# Revit family: Rohrschelle Titan HD, halb Zoll, Silikon
name_source: partatom
category: HLS-Bauteile
revit_build: Autodesk Revit 2017 (Build: 20190507_1515(x64)
units: mm (PartAtom-declared; Revit-internal decimal feet)

## family parameters
Arbeitsebenenbasiert = Ja
Beim Laden mit Abzugskörper schneiden = Nein
Bemaßung runder Anschluss = Durchmesser verwenden
Gemeinsam genutzt = Ja
Immer vertikal = Nein
Raumberechnungspunkt = Nein
Teiletyp = Normal

## types (30) — shared parameters
A = 26 mm  [stored 0.0853018 ft]
DF1 = 29 mm  [stored 0.0951444 ft]
DS = 6 mm  [stored 0.019685 ft]
DVS = 13 mm
Firma = MEFA Befestigungs- und Montagesysteme GmbH
HGA = 15 mm  [stored 0.0492126 ft]
MB = 50 mm  [stored 0.164042 ft]
MD = 5 mm  [stored 0.0164042 ft]
Vorgabe-Ansicht = 1219 mm
max. zul. Last horizontal = 0.00 kN
max. zul. Last vertikal = 0.00 kN
zero-valued in all types: Nennweite DN Rohr, Stärke Material, max. Rohraußendurchmesser, min. Rohraußendurchmesser

## per-type parameters (varying)
- Titan HD, 1/2", Ø 64, Silikon: Achsabstand=125 mm; Anschluss=1/2''; Anschlußhöhe=26 mm; Artikelnummer=0077506; B=154 mm; Bauart=zweiteilig; Baustoffklasse=B2; Brandschutz=RAL GZ 656; Breite=154 mm; D=64 mm  [stored 0.209974 ft]; D0=76 mm  [stored 0.249344 ft]; DF2=19 mm  [stored 0.062336 ft]; Dämmstärke=6 mm  [stored 0.019685 ft]; EAN=4250928405203; Fabrikat=MEFA; Farbe Schalldämmeinlage=rot; Gewicht=0.93 kg; Gewicht pro Bauteil=0.93 kg; H=101 mm; Höhe=101 mm; Kurztext1=Rohrschelle Titan HD 50x5,0; Kurztext2=64 mm 1/2'' Silikon; Material=Stahl; Material Schalldämmeinlage=Silikon; Materialmaße=50x5,0 mm; Materialname=S235; Mengeneinheit=St; Oberflaeche=galvanisch verzinkt; R=38 mm  [stored 0.124672 ft]; RM=43 mm; Rohraußendurchmesser=64 mm  [stored 0.209974 ft]; Rohraußendurchmesser Zoll=Zoll; S=125 mm; Schalldämmeinlage=Silikon; Verschluss=Schraubverschluss; Verschluss-Schraube=M12; max. Höhe=101 mm; max. Temperaturbeständigkeit=250 °C; max. zul. Last=3.20 kN; vpe=1 St
- Titan HD, 1/2", Ø 76, Silikon: Achsabstand=137 mm; Anschluss=1/2''; Anschlußhöhe=26 mm; Artikelnummer=0077510; B=166 mm; Bauart=zweiteilig; Baustoffklasse=B2; Brandschutz=RAL GZ 656; Breite=166 mm; D=76 mm  [stored 0.249344 ft]; D0=88 mm  [stored 0.288714 ft]; DF2=19 mm  [stored 0.062336 ft]; Dämmstärke=6 mm  [stored 0.019685 ft]; EAN=4250928405210; Fabrikat=MEFA; Farbe Schalldämmeinlage=rot; Gewicht=1.02 kg; Gewicht pro Bauteil=1.02 kg; H=113 mm; Höhe=113 mm; Kurztext1=Rohrschelle Titan HD 50x5,0; Kurztext2=76 mm 1/2'' Silikon; Material=Stahl; Material Schalldämmeinlage=Silikon; Materialmaße=50x5,0 mm; Materialname=S235; Mengeneinheit=St; Oberflaeche=galvanisch verzinkt; R=44 mm  [stored 0.144357 ft]; RM=49 mm; Rohraußendurchmesser=76 mm  [stored 0.249344 ft]; Rohraußendurchmesser Zoll=2 1/2 Zoll; S=137 mm; Schalldämmeinlage=Silikon; Verschluss=Schraubverschluss; Verschluss-Schraube=M12; max. Höhe=113 mm; max. Temperaturbeständigkeit=250 °C; max. zul. Last=3.20 kN; vpe=1 St
- Titan HD, 1/2", Ø 89, Silikon: Artikelnummer=0077512; B=179 mm; Breite=0 mm  [stored 0 ft]; D=89 mm  [stored 0.291995 ft]; D0=101 mm; DF2=19 mm  [stored 0.062336 ft]; Dämmstärke=0 mm  [stored 0 ft]; Gewicht=0.00 kg; Gewicht pro Bauteil=0.00 kg; H=126 mm; R=51 mm; RM=56 mm; Rohraußendurchmesser=0 mm  [stored 0 ft]; S=150 mm; max. Höhe=0 mm  [stored 0 ft]; max. zul. Last=0.00 kN
- Titan HD, 1/2", Ø108, Silikon: Achsabstand=170 mm; Anschluss=1/2''; Anschlußhöhe=26 mm; Artikelnummer=0077518; B=199 mm; Bauart=zweiteilig; Baustoffklasse=B2; Brandschutz=RAL GZ 656; Breite=199 mm; D=108 mm; D0=120 mm; DF2=20 mm  [stored 0.0656168 ft]; Dämmstärke=6 mm  [stored 0.019685 ft]; EAN=4250928405234; Fabrikat=MEFA; Farbe Schalldämmeinlage=rot; Gewicht=1.26 kg; Gewicht pro Bauteil=1.26 kg; H=145 mm; Höhe=145 mm; Kurztext1=Rohrschelle Titan HD 50x5,0; Kurztext2=108 mm 1/2'' Silikon; Material=Stahl; Material Schalldämmeinlage=Silikon; Materialmaße=50x5,0 mm; Materialname=S235; Mengeneinheit=St; Oberflaeche=galvanisch verzinkt; R=60 mm  [stored 0.19685 ft]; RM=65 mm; Rohraußendurchmesser=108 mm; Rohraußendurchmesser Zoll=Zoll; S=170 mm; Schalldämmeinlage=Silikon; Verschluss=Schraubverschluss; Verschluss-Schraube=M12; max. Höhe=145 mm; max. Temperaturbeständigkeit=250 °C; max. zul. Last=3.20 kN; vpe=1 St
- Titan HD, 1/2", Ø110, Silikon: Achsabstand=172 mm; Anschluss=1/2''; Anschlußhöhe=26 mm; Artikelnummer=0077534; B=201 mm; Bauart=zweiteilig; Baustoffklasse=B2; Brandschutz=RAL GZ 656; Breite=201 mm; D=110 mm; D0=122 mm; DF2=20 mm  [stored 0.0656168 ft]; Dämmstärke=6 mm  [stored 0.019685 ft]; EAN=4250928405241; Fabrikat=MEFA; Farbe Schalldämmeinlage=rot; Gewicht=1.28 kg; Gewicht pro Bauteil=1.28 kg; H=147 mm; Höhe=147 mm; Kurztext1=Rohrschelle Titan HD 50x5,0; Kurztext2=110 mm 1/2'' Silikon; Material=Stahl; Material Schalldämmeinlage=Silikon; Materialmaße=50x5,0 mm; Materialname=S235; Mengeneinheit=St; Oberflaeche=galvanisch verzinkt; R=61 mm  [stored 0.200131 ft]; RM=66 mm; Rohraußendurchmesser=110 mm; Rohraußendurchmesser Zoll=Zoll; S=172 mm; Schalldämmeinlage=Silikon; Verschluss=Schraubverschluss; Verschluss-Schraube=M12; max. Höhe=147 mm; max. Temperaturbeständigkeit=250 °C; max. zul. Last=3.20 kN; vpe=1 St
- Titan HD, 1/2", Ø133, Silikon: Achsabstand=195 mm; Anschluss=1/2''; Anschlußhöhe=26 mm; Artikelnummer=0077607; B=224 mm; Bauart=zweiteilig; Baustoffklasse=B2; Brandschutz=RAL GZ 656; Breite=224 mm; D=133 mm; D0=145 mm; DF2=20 mm  [stored 0.0656168 ft]; Dämmstärke=6 mm  [stored 0.019685 ft]; EAN=4250928405289; Fabrikat=MEFA; Farbe Schalldämmeinlage=rot; Gewicht=1.45 kg; Gewicht pro Bauteil=1.45 kg; H=170 mm; Höhe=170 mm; Kurztext1=Rohrschelle Titan HD 50x5,0; Kurztext2=133 mm 1/2'' Silikon; Material=Stahl; Material Schalldämmeinlage=Silikon; Materialmaße=50x5,0 mm; Materialname=S235; Mengeneinheit=St; Oberflaeche=galvanisch verzinkt; R=73 mm; RM=78 mm; Rohraußendurchmesser=133 mm; Rohraußendurchmesser Zoll=Zoll; S=195 mm; Schalldämmeinlage=Silikon; Verschluss=Schraubverschluss; Verschluss-Schraube=M12; max. Höhe=170 mm; max. Temperaturbeständigkeit=250 °C; max. zul. Last=3.20 kN; vpe=1 St
- Titan HD, 1/2", Ø135, Silikon: Achsabstand=197 mm; Anschluss=1/2''; Anschlußhöhe=26 mm; Artikelnummer=0077615; B=226 mm; Bauart=zweiteilig; Baustoffklasse=B2; Brandschutz=RAL GZ 656; Breite=226 mm; D=135 mm; D0=147 mm; DF2=20 mm  [stored 0.0656168 ft]; Dämmstärke=6 mm  [stored 0.019685 ft]; EAN=4250928405296; Fabrikat=MEFA; Farbe Schalldämmeinlage=rot; Gewicht=1.46 kg; Gewicht pro Bauteil=1.46 kg; H=172 mm; Höhe=172 mm; Kurztext1=Rohrschelle Titan HD 50x5,0; Kurztext2=135 mm 1/2'' Silikon; Material=Stahl; Material Schalldämmeinlage=Silikon; Materialmaße=50x5,0 mm; Materialname=S235; Mengeneinheit=St; Oberflaeche=galvanisch verzinkt; R=74 mm; RM=79 mm; Rohraußendurchmesser=135 mm; Rohraußendurchmesser Zoll=Zoll; S=197 mm; Schalldämmeinlage=Silikon; Verschluss=Schraubverschluss; Verschluss-Schraube=M12; max. Höhe=172 mm; max. Temperaturbeständigkeit=250 °C; max. zul. Last=3.20 kN; vpe=1 St
- Titan HD, 1/2", Ø140, Silikon: Achsabstand=202 mm; Anschluss=1/2''; Anschlußhöhe=26 mm; Artikelnummer=0077623; B=231 mm; Bauart=zweiteilig; Baustoffklasse=B2; Brandschutz=RAL GZ 656; Breite=231 mm; D=140 mm; D0=152 mm; DF2=20 mm  [stored 0.0656168 ft]; Dämmstärke=6 mm  [stored 0.019685 ft]; EAN=4250928405302; Fabrikat=MEFA; Farbe Schalldämmeinlage=rot; Gewicht=1.50 kg; Gewicht pro Bauteil=1.50 kg; H=177 mm; Höhe=177 mm; Kurztext1=Rohrschelle Titan HD 50x5,0; Kurztext2=140 mm 1/2'' Silikon; Material=Stahl; Material Schalldämmeinlage=Silikon; Materialmaße=50x5,0 mm; Materialname=S235; Mengeneinheit=St; Oberflaeche=galvanisch verzinkt; R=76 mm  [stored 0.249344 ft]; RM=81 mm  [stored 0.265748 ft]; Rohraußendurchmesser=140 mm; Rohraußendurchmesser Zoll=5 Zoll; S=202 mm; Schalldämmeinlage=Silikon; Verschluss=Schraubverschluss; Verschluss-Schraube=M12; max. Höhe=177 mm; max. Temperaturbeständigkeit=250 °C; max. zul. Last=3.20 kN; vpe=1 St
- Titan HD, 1/2", Ø160, Silikon: Achsabstand=222 mm; Anschluss=1/2''; Anschlußhöhe=26 mm; Artikelnummer=0077682; B=251 mm; Bauart=zweiteilig; Baustoffklasse=B2; Brandschutz=RAL GZ 656; Breite=251 mm; D=160 mm; D0=172 mm; DF2=20 mm  [stored 0.0656168 ft]; Dämmstärke=6 mm  [stored 0.019685 ft]; EAN=4250928405326; Fabrikat=MEFA; Farbe Schalldämmeinlage=rot; Gewicht=1.65 kg; Gewicht pro Bauteil=1.65 kg; H=197 mm; Höhe=197 mm; Kurztext1=Rohrschelle Titan HD 50x5,0; Kurztext2=160 mm 1/2'' Silikon; Material=Stahl; Material Schalldämmeinlage=Silikon; Materialmaße=50x5,0 mm; Materialname=S235; Mengeneinheit=St; Oberflaeche=galvanisch verzinkt; R=86 mm  [stored 0.282152 ft]; RM=91 mm  [stored 0.298556 ft]; Rohraußendurchmesser=160 mm; Rohraußendurchmesser Zoll=Zoll; S=222 mm; Schalldämmeinlage=Silikon; Verschluss=Schraubverschluss; Verschluss-Schraube=M12; max. Höhe=197 mm; max. Temperaturbeständigkeit=250 °C; max. zul. Last=3.20 kN; vpe=1 St
- Titan HD, 1/2", Ø165, Silikon: Achsabstand=227 mm; Anschluss=1/2''; Anschlußhöhe=26 mm; Artikelnummer=0077690; B=256 mm; Bauart=zweiteilig; Baustoffklasse=B2; Brandschutz=RAL GZ 656; Breite=256 mm; D=165 mm; D0=177 mm; DF2=20 mm  [stored 0.0656168 ft]; Dämmstärke=6 mm  [stored 0.019685 ft]; EAN=4250928405333; Fabrikat=MEFA; Farbe Schalldämmeinlage=rot; Gewicht=1.69 kg; Gewicht pro Bauteil=1.69 kg; H=202 mm; Höhe=202 mm; Kurztext1=Rohrschelle Titan HD 50x5,0; Kurztext2=165 mm 1/2'' Silikon; Material=Stahl; Material Schalldämmeinlage=Silikon; Materialmaße=50x5,0 mm; Materialname=S235; Mengeneinheit=St; Oberflaeche=galvanisch verzinkt; R=89 mm  [stored 0.291995 ft]; RM=94 mm; Rohraußendurchmesser=165 mm; Rohraußendurchmesser Zoll=6 Zoll; S=227 mm; Schalldämmeinlage=Silikon; Verschluss=Schraubverschluss; Verschluss-Schraube=M12; max. Höhe=202 mm; max. Temperaturbeständigkeit=250 °C; max. zul. Last=3.20 kN; vpe=1 St
- Titan HD, 1/2", Ø168, Silikon: Achsabstand=230 mm; Anschluss=1/2''; Anschlußhöhe=26 mm; Artikelnummer=0077712; B=259 mm; Bauart=zweiteilig; Baustoffklasse=B2; Brandschutz=RAL GZ 656; Breite=259 mm; D=168 mm; D0=180 mm; DF2=20 mm  [stored 0.0656168 ft]; Dämmstärke=6 mm  [stored 0.019685 ft]; EAN=4250928405340; Fabrikat=MEFA; Farbe Schalldämmeinlage=rot; Gewicht=1.71 kg; Gewicht pro Bauteil=1.71 kg; H=205 mm; Höhe=205 mm; Kurztext1=Rohrschelle Titan HD 50x5,0; Kurztext2=168 mm 1/2'' Silikon; Material=Stahl; Material Schalldämmeinlage=Silikon; Materialmaße=50x5,0 mm; Materialname=S235; Mengeneinheit=St; Oberflaeche=galvanisch verzinkt; R=90 mm; RM=95 mm; Rohraußendurchmesser=168 mm; Rohraußendurchmesser Zoll=Zoll; S=230 mm; Schalldämmeinlage=Silikon; Verschluss=Schraubverschluss; Verschluss-Schraube=M12; max. Höhe=205 mm; max. Temperaturbeständigkeit=250 °C; max. zul. Last=3.20 kN; vpe=1 St
- Titan HD, 1/2", Ø194, Silikon: Achsabstand=257 mm; Anschluss=1/2''; Anschlußhöhe=26 mm; Artikelnummer=0077771; B=286 mm; Bauart=zweiteilig; Baustoffklasse=B2; Brandschutz=RAL GZ 656; Breite=286 mm; D=194 mm; D0=206 mm; DF2=20 mm  [stored 0.0656168 ft]; Dämmstärke=6 mm  [stored 0.019685 ft]; EAN=4250928405371; Fabrikat=MEFA; Farbe Schalldämmeinlage=rot; Gewicht=1.91 kg; Gewicht pro Bauteil=1.91 kg; H=231 mm; Höhe=231 mm; Kurztext1=Rohrschelle Titan HD 50x5,0; Kurztext2=194 mm 1/2'' Silikon; Material=Stahl; Material Schalldämmeinlage=Silikon; Materialmaße=50x5,0 mm; Materialname=S235; Mengeneinheit=St; Oberflaeche=galvanisch verzinkt; R=103 mm; RM=108 mm; Rohraußendurchmesser=194 mm; Rohraußendurchmesser Zoll=Zoll; S=257 mm; Schalldämmeinlage=Silikon; Verschluss=Schraubverschluss; Verschluss-Schraube=M12; max. Höhe=231 mm; max. Temperaturbeständigkeit=250 °C; max. zul. Last=11.50 kN; vpe=1 St
- Titan HD, 1/2", Ø200, Silikon: Achsabstand=263 mm; Anschluss=1/2''; Anschlußhöhe=26 mm; Artikelnummer=0077798; B=292 mm; Bauart=zweiteilig; Baustoffklasse=B2; Brandschutz=RAL GZ 656; Breite=292 mm; D=200 mm; D0=212 mm; DF2=20 mm  [stored 0.0656168 ft]; Dämmstärke=6 mm  [stored 0.019685 ft]; EAN=4250928405388; Fabrikat=MEFA; Farbe Schalldämmeinlage=rot; Gewicht=1.95 kg; Gewicht pro Bauteil=1.95 kg; H=237 mm; Höhe=237 mm; Kurztext1=Rohrschelle Titan HD 50x5,0; Kurztext2=200 mm 1/2'' Silikon; Material=Stahl; Material Schalldämmeinlage=Silikon; Materialmaße=50x5,0 mm; Materialname=S235; Mengeneinheit=St; Oberflaeche=galvanisch verzinkt; R=106 mm; RM=111 mm; Rohraußendurchmesser=200 mm; Rohraußendurchmesser Zoll=Zoll; S=263 mm; Schalldämmeinlage=Silikon; Verschluss=Schraubverschluss; Verschluss-Schraube=M12; max. Höhe=237 mm; max. Temperaturbeständigkeit=250 °C; max. zul. Last=11.50 kN; vpe=1 St
- Titan HD, 1/2", Ø210, Silikon: Achsabstand=273 mm; Anschluss=1/2''; Anschlußhöhe=26 mm; Artikelnummer=0077801; B=302 mm; Bauart=zweiteilig; Baustoffklasse=B2; Brandschutz=RAL GZ 656; Breite=302 mm; D=210 mm; D0=222 mm; DF2=20 mm  [stored 0.0656168 ft]; Dämmstärke=6 mm  [stored 0.019685 ft]; EAN=4250928405395; Fabrikat=MEFA; Farbe Schalldämmeinlage=rot; Gewicht=2.03 kg; Gewicht pro Bauteil=2.03 kg; H=247 mm; Höhe=247 mm; Kurztext1=Rohrschelle Titan HD 50x5,0; Kurztext2=210 mm 1/2'' Silikon; Material=Stahl; Material Schalldämmeinlage=Silikon; Materialmaße=50x5,0 mm; Materialname=S235; Mengeneinheit=St; Oberflaeche=galvanisch verzinkt; R=111 mm; RM=116 mm; Rohraußendurchmesser=210 mm; Rohraußendurchmesser Zoll=Zoll; S=273 mm; Schalldämmeinlage=Silikon; Verschluss=Schraubverschluss; Verschluss-Schraube=M12; max. Höhe=247 mm; max. Temperaturbeständigkeit=250 °C; max. zul. Last=11.50 kN; vpe=1 St
- Titan HD, 1/2", Ø219, Silikon: Achsabstand=282 mm; Anschluss=1/2''; Anschlußhöhe=26 mm; Artikelnummer=0077828; B=311 mm; Bauart=zweiteilig; Baustoffklasse=B2; Brandschutz=RAL GZ 656; Breite=311 mm; D=219 mm; D0=231 mm; DF2=20 mm  [stored 0.0656168 ft]; Dämmstärke=6 mm  [stored 0.019685 ft]; EAN=4250928405401; Fabrikat=MEFA; Farbe Schalldämmeinlage=rot; Gewicht=2.09 kg; Gewicht pro Bauteil=2.09 kg; H=256 mm; Höhe=256 mm; Kurztext1=Rohrschelle Titan HD 50x5,0; Kurztext2=219 mm 1/2'' Silikon; Material=Stahl; Material Schalldämmeinlage=Silikon; Materialmaße=50x5,0 mm; Materialname=S235; Mengeneinheit=St; Oberflaeche=galvanisch verzinkt; R=116 mm; RM=121 mm; Rohraußendurchmesser=219 mm; Rohraußendurchmesser Zoll=8 Zoll; S=282 mm; Schalldämmeinlage=Silikon; Verschluss=Schraubverschluss; Verschluss-Schraube=M12; max. Höhe=256 mm; max. Temperaturbeständigkeit=250 °C; max. zul. Last=11.50 kN; vpe=1 St
- Titan HD, 1/2", Ø267, Silikon: Achsabstand=330 mm; Anschluss=1/2''; Anschlußhöhe=26 mm; Artikelnummer=0077895; B=359 mm; Bauart=zweiteilig; Baustoffklasse=B2; Brandschutz=RAL GZ 656; Breite=359 mm; D=267 mm; D0=279 mm; DF2=20 mm  [stored 0.0656168 ft]; Dämmstärke=6 mm  [stored 0.019685 ft]; EAN=4250928405432; Fabrikat=MEFA; Farbe Schalldämmeinlage=rot; Gewicht=2.45 kg; Gewicht pro Bauteil=2.45 kg; H=304 mm; Höhe=304 mm; Kurztext1=Rohrschelle Titan HD 50x5,0; Kurztext2=267 mm 1/2'' Silikon; Material=Stahl; Material Schalldämmeinlage=Silikon; Materialmaße=50x5,0 mm; Materialname=S235; Mengeneinheit=St; Oberflaeche=galvanisch verzinkt; R=140 mm; RM=145 mm; Rohraußendurchmesser=267 mm; Rohraußendurchmesser Zoll=Zoll; S=330 mm; Schalldämmeinlage=Silikon; Verschluss=Schraubverschluss; Verschluss-Schraube=M12; max. Höhe=304 mm; max. Temperaturbeständigkeit=250 °C; max. zul. Last=11.50 kN; vpe=1 St
- Titan HD, 1/2", Ø273, Silikon: Achsabstand=336 mm; Anschluss=1/2''; Anschlußhöhe=26 mm; Artikelnummer=0077909; B=365 mm; Bauart=zweiteilig; Baustoffklasse=B2; Brandschutz=RAL GZ 656; Breite=365 mm; D=273 mm; D0=285 mm; DF2=20 mm  [stored 0.0656168 ft]; Dämmstärke=6 mm  [stored 0.019685 ft]; EAN=4250928405449; Fabrikat=MEFA; Farbe Schalldämmeinlage=rot; Gewicht=2.50 kg; Gewicht pro Bauteil=2.50 kg; H=310 mm; Höhe=310 mm; Kurztext1=Rohrschelle Titan HD 50x5,0; Kurztext2=273 mm 1/2'' Silikon; Material=Stahl; Material Schalldämmeinlage=Silikon; Materialmaße=50x5,0 mm; Materialname=S235; Mengeneinheit=St; Oberflaeche=galvanisch verzinkt; R=143 mm; RM=148 mm; Rohraußendurchmesser=273 mm; Rohraußendurchmesser Zoll=10 Zoll; S=336 mm; Schalldämmeinlage=Silikon; Verschluss=Schraubverschluss; Verschluss-Schraube=M12; max. Höhe=310 mm; max. Temperaturbeständigkeit=250 °C; max. zul. Last=11.50 kN; vpe=1 St
- Titan HD, 1/2", Ø324, Silikon: Achsabstand=387 mm; Anschluss=1/2''; Anschlußhöhe=26 mm; Artikelnummer=0077941; B=416 mm; Bauart=zweiteilig; Baustoffklasse=B2; Brandschutz=RAL GZ 656; Breite=416 mm; D=324 mm; D0=336 mm; DF2=20 mm  [stored 0.0656168 ft]; Dämmstärke=6 mm  [stored 0.019685 ft]; EAN=4250928405470; Fabrikat=MEFA; Farbe Schalldämmeinlage=rot; Gewicht=2.88 kg; Gewicht pro Bauteil=2.88 kg; H=361 mm; Höhe=361 mm; Kurztext1=Rohrschelle Titan HD 50x5,0; Kurztext2=324 mm 1/2'' Silikon; Material=Stahl; Material Schalldämmeinlage=Silikon; Materialmaße=50x5,0 mm; Materialname=S235; Mengeneinheit=St; Oberflaeche=galvanisch verzinkt; R=168 mm; RM=173 mm; Rohraußendurchmesser=324 mm; Rohraußendurchmesser Zoll=12 Zoll; S=387 mm; Schalldämmeinlage=Silikon; Verschluss=Schraubverschluss; Verschluss-Schraube=M12; max. Höhe=361 mm; max. Temperaturbeständigkeit=250 °C; max. zul. Last=11.50 kN; vpe=1 St
- Titan HD, 1/2", Ø356, Silikon: Achsabstand=419 mm; Anschluss=1/2''; Anschlußhöhe=26 mm; Artikelnummer=0077968; B=448 mm; Bauart=zweiteilig; Baustoffklasse=B2; Brandschutz=RAL GZ 656; Breite=448 mm; D=356 mm; D0=368 mm; DF2=20 mm  [stored 0.0656168 ft]; Dämmstärke=6 mm  [stored 0.019685 ft]; EAN=4250928405487; Fabrikat=MEFA; Farbe Schalldämmeinlage=rot; Gewicht=3.12 kg; Gewicht pro Bauteil=3.12 kg; H=393 mm; Höhe=393 mm; Kurztext1=Rohrschelle Titan HD 50x5,0; Kurztext2=356 mm 1/2'' Silikon; Material=Stahl; Material Schalldämmeinlage=Silikon; Materialmaße=50x5,0 mm; Materialname=S235; Mengeneinheit=St; Oberflaeche=galvanisch verzinkt; R=184 mm; RM=189 mm; Rohraußendurchmesser=356 mm; Rohraußendurchmesser Zoll=Zoll; S=419 mm; Schalldämmeinlage=Silikon; Verschluss=Schraubverschluss; Verschluss-Schraube=M12; max. Höhe=393 mm; max. Temperaturbeständigkeit=250 °C; max. zul. Last=11.50 kN; vpe=1 St
- Titan HD, 1/2", Ø368, Silikon: Achsabstand=431 mm; Anschluss=1/2''; Anschlußhöhe=26 mm; Artikelnummer=0077984; B=460 mm; Bauart=zweiteilig; Baustoffklasse=B2; Brandschutz=RAL GZ 656; Breite=460 mm; D=368 mm; D0=380 mm; DF2=20 mm  [stored 0.0656168 ft]; Dämmstärke=6 mm  [stored 0.019685 ft]; EAN=4250928405494; Fabrikat=MEFA; Farbe Schalldämmeinlage=rot; Gewicht=3.21 kg; Gewicht pro Bauteil=3.21 kg; H=405 mm; Höhe=405 mm; Kurztext1=Rohrschelle Titan HD 50x5,0; Kurztext2=368 mm 1/2'' Silikon; Material=Stahl; Material Schalldämmeinlage=Silikon; Materialmaße=50x5,0 mm; Materialname=S235; Mengeneinheit=St; Oberflaeche=galvanisch verzinkt; R=190 mm; RM=195 mm; Rohraußendurchmesser=368 mm; Rohraußendurchmesser Zoll=Zoll; S=431 mm; Schalldämmeinlage=Silikon; Verschluss=Schraubverschluss; Verschluss-Schraube=M12; max. Höhe=405 mm; max. Temperaturbeständigkeit=250 °C; max. zul. Last=11.50 kN; vpe=1 St
- Titan HD, 1/2", Ø114, Silikon: Achsabstand=176 mm; Anschluss=1/2''; Anschlußhöhe=26 mm; Artikelnummer=0077550; B=205 mm; Bauart=zweiteilig; Baustoffklasse=B2; Brandschutz=RAL GZ 656; Breite=205 mm; D=114 mm; D0=126 mm; DF2=20 mm  [stored 0.0656168 ft]; Dämmstärke=6 mm  [stored 0.019685 ft]; EAN=4250928405258; Fabrikat=MEFA; Farbe Schalldämmeinlage=rot; Gewicht=1.31 kg; Gewicht pro Bauteil=1.31 kg; H=151 mm; Höhe=151 mm; Kurztext1=Rohrschelle Titan HD 50x5,0; Kurztext2=114 mm 1/2'' Silikon; Material=Stahl; Material Schalldämmeinlage=Silikon; Materialmaße=50x5,0 mm; Materialname=S235; Mengeneinheit=St; Oberflaeche=galvanisch verzinkt; R=63 mm  [stored 0.206693 ft]; RM=68 mm  [stored 0.223097 ft]; Rohraußendurchmesser=114 mm; Rohraußendurchmesser Zoll=4 Zoll; S=176 mm; Schalldämmeinlage=Silikon; Verschluss=Schraubverschluss; Verschluss-Schraube=M12; max. Höhe=151 mm; max. Temperaturbeständigkeit=250 °C; max. zul. Last=3.20 kN; vpe=1 St
- Titan HD, 1/2", Ø125, Silikon: Achsabstand=187 mm; Anschluss=1/2''; Anschlußhöhe=26 mm; Artikelnummer=0077585; B=216 mm; Bauart=zweiteilig; Baustoffklasse=B2; Brandschutz=RAL GZ 656; Breite=216 mm; D=125 mm; D0=137 mm; DF2=20 mm  [stored 0.0656168 ft]; Dämmstärke=6 mm  [stored 0.019685 ft]; EAN=4250928405265; Fabrikat=MEFA; Farbe Schalldämmeinlage=rot; Gewicht=1.39 kg; Gewicht pro Bauteil=1.39 kg; H=162 mm; Höhe=162 mm; Kurztext1=Rohrschelle Titan HD 50x5,0; Kurztext2=125 mm 1/2'' Silikon; Material=Stahl; Material Schalldämmeinlage=Silikon; Materialmaße=50x5,0 mm; Materialname=S235; Mengeneinheit=St; Oberflaeche=galvanisch verzinkt; R=69 mm; RM=74 mm; Rohraußendurchmesser=125 mm; Rohraußendurchmesser Zoll=Zoll; S=187 mm; Schalldämmeinlage=Silikon; Verschluss=Schraubverschluss; Verschluss-Schraube=M12; max. Höhe=162 mm; max. Temperaturbeständigkeit=250 °C; max. zul. Last=3.20 kN; vpe=1 St
- Titan HD, 1/2", Ø127, Silikon: Achsabstand=189 mm; Anschluss=1/2''; Anschlußhöhe=26 mm; Artikelnummer=0077593; B=218 mm; Bauart=zweiteilig; Baustoffklasse=B2; Brandschutz=RAL GZ 656; Breite=218 mm; D=127 mm; D0=139 mm; DF2=20 mm  [stored 0.0656168 ft]; Dämmstärke=6 mm  [stored 0.019685 ft]; EAN=4250928405272; Fabrikat=MEFA; Farbe Schalldämmeinlage=rot; Gewicht=1.40 kg; Gewicht pro Bauteil=1.40 kg; H=164 mm; Höhe=164 mm; Kurztext1=Rohrschelle Titan HD 50x5,0; Kurztext2=127 mm 1/2'' Silikon; Material=Stahl; Material Schalldämmeinlage=Silikon; Materialmaße=50x5,0 mm; Materialname=S235; Mengeneinheit=St; Oberflaeche=galvanisch verzinkt; R=70 mm; RM=75 mm; Rohraußendurchmesser=127 mm; Rohraußendurchmesser Zoll=Zoll; S=189 mm; Schalldämmeinlage=Silikon; Verschluss=Schraubverschluss; Verschluss-Schraube=M12; max. Höhe=164 mm; max. Temperaturbeständigkeit=250 °C; max. zul. Last=3.20 kN; vpe=1 St
- Titan HD, 1/2", Ø152, Silikon: Achsabstand=214 mm; Anschluss=1/2''; Anschlußhöhe=26 mm; Artikelnummer=0077631; B=243 mm; Bauart=zweiteilig; Baustoffklasse=B2; Brandschutz=RAL GZ 656; Breite=243 mm; D=152 mm; D0=164 mm; DF2=20 mm  [stored 0.0656168 ft]; Dämmstärke=6 mm  [stored 0.019685 ft]; EAN=4250928405319; Fabrikat=MEFA; Farbe Schalldämmeinlage=rot; Gewicht=1.59 kg; Gewicht pro Bauteil=1.59 kg; H=189 mm; Höhe=189 mm; Kurztext1=Rohrschelle Titan HD 50x5,0; Kurztext2=152 mm 1/2'' Silikon; Material=Stahl; Material Schalldämmeinlage=Silikon; Materialmaße=50x5,0 mm; Materialname=S235; Mengeneinheit=St; Oberflaeche=galvanisch verzinkt; R=82 mm  [stored 0.269029 ft]; RM=87 mm  [stored 0.285433 ft]; Rohraußendurchmesser=152 mm; Rohraußendurchmesser Zoll=Zoll; S=214 mm; Schalldämmeinlage=Silikon; Verschluss=Schraubverschluss; Verschluss-Schraube=M12; max. Höhe=189 mm; max. Temperaturbeständigkeit=250 °C; max. zul. Last=3.20 kN; vpe=1 St
- Titan HD, 1/2", Ø177, Silikon: Achsabstand=239 mm; Anschluss=1/2''; Anschlußhöhe=26 mm; Artikelnummer=0077739; B=268 mm; Bauart=zweiteilig; Baustoffklasse=B2; Brandschutz=RAL GZ 656; Breite=268 mm; D=177 mm; D0=189 mm; DF2=20 mm  [stored 0.0656168 ft]; Dämmstärke=6 mm  [stored 0.019685 ft]; EAN=4250928405357; Fabrikat=MEFA; Farbe Schalldämmeinlage=rot; Gewicht=1.78 kg; Gewicht pro Bauteil=1.78 kg; H=214 mm; Höhe=214 mm; Kurztext1=Rohrschelle Titan HD 50x5,0; Kurztext2=177 mm 1/2'' Silikon; Material=Stahl; Material Schalldämmeinlage=Silikon; Materialmaße=50x5,0 mm; Materialname=S235; Mengeneinheit=St; Oberflaeche=galvanisch verzinkt; R=95 mm; RM=100 mm; Rohraußendurchmesser=177 mm; Rohraußendurchmesser Zoll=Zoll; S=239 mm; Schalldämmeinlage=Silikon; Verschluss=Schraubverschluss; Verschluss-Schraube=M12; max. Höhe=214 mm; max. Temperaturbeständigkeit=250 °C; max. zul. Last=11.50 kN; vpe=1 St
- Titan HD, 1/2", Ø180, Silikon: Achsabstand=242 mm; Anschluss=1/2''; Anschlußhöhe=26 mm; Artikelnummer=0077755; B=271 mm; Bauart=zweiteilig; Baustoffklasse=B2; Brandschutz=RAL GZ 656; Breite=271 mm; D=180 mm; D0=192 mm; DF2=20 mm  [stored 0.0656168 ft]; Dämmstärke=6 mm  [stored 0.019685 ft]; EAN=4250928405364; Fabrikat=MEFA; Farbe Schalldämmeinlage=rot; Gewicht=1.80 kg; Gewicht pro Bauteil=1.80 kg; H=217 mm; Höhe=217 mm; Kurztext1=Rohrschelle Titan HD 50x5,0; Kurztext2=180 mm 1/2'' Silikon; Material=Stahl; Material Schalldämmeinlage=Silikon; Materialmaße=50x5,0 mm; Materialname=S235; Mengeneinheit=St; Oberflaeche=galvanisch verzinkt; R=96 mm; RM=101 mm; Rohraußendurchmesser=180 mm; Rohraußendurchmesser Zoll=Zoll; S=242 mm; Schalldämmeinlage=Silikon; Verschluss=Schraubverschluss; Verschluss-Schraube=M12; max. Höhe=217 mm; max. Temperaturbeständigkeit=250 °C; max. zul. Last=11.50 kN; vpe=1 St
- Titan HD, 1/2", Ø225, Silikon: Achsabstand=288 mm; Anschluss=1/2''; Anschlußhöhe=26 mm; Artikelnummer=0077844; B=317 mm; Bauart=zweiteilig; Baustoffklasse=B2; Brandschutz=RAL GZ 656; Breite=317 mm; D=225 mm; D0=237 mm; DF2=20 mm  [stored 0.0656168 ft]; Dämmstärke=6 mm  [stored 0.019685 ft]; EAN=4250928405418; Fabrikat=MEFA; Farbe Schalldämmeinlage=rot; Gewicht=2.14 kg; Gewicht pro Bauteil=2.14 kg; H=262 mm; Höhe=262 mm; Kurztext1=Rohrschelle Titan HD 50x5,0; Kurztext2=225 mm 1/2'' Silikon; Material=Stahl; Material Schalldämmeinlage=Silikon; Materialmaße=50x5,0 mm; Materialname=S235; Mengeneinheit=St; Oberflaeche=galvanisch verzinkt; R=119 mm; RM=124 mm; Rohraußendurchmesser=225 mm; Rohraußendurchmesser Zoll=Zoll; S=288 mm; Schalldämmeinlage=Silikon; Verschluss=Schraubverschluss; Verschluss-Schraube=M12; max. Höhe=262 mm; max. Temperaturbeständigkeit=250 °C; max. zul. Last=11.50 kN; vpe=1 St
- Titan HD, 1/2", Ø245, Silikon: Achsabstand=308 mm; Anschluss=1/2''; Anschlußhöhe=26 mm; Artikelnummer=0077879; B=337 mm; Bauart=zweiteilig; Baustoffklasse=B2; Brandschutz=RAL GZ 656; Breite=337 mm; D=245 mm; D0=257 mm; DF2=20 mm  [stored 0.0656168 ft]; Dämmstärke=6 mm  [stored 0.019685 ft]; EAN=4250928405425; Fabrikat=MEFA; Farbe Schalldämmeinlage=rot; Gewicht=2.29 kg; Gewicht pro Bauteil=2.29 kg; H=282 mm; Höhe=282 mm; Kurztext1=Rohrschelle Titan HD 50x5,0; Kurztext2=245 mm 1/2'' Silikon; Material=Stahl; Material Schalldämmeinlage=Silikon; Materialmaße=50x5,0 mm; Materialname=S235; Mengeneinheit=St; Oberflaeche=galvanisch verzinkt; R=129 mm; RM=134 mm; Rohraußendurchmesser=245 mm; Rohraußendurchmesser Zoll=Zoll; S=308 mm; Schalldämmeinlage=Silikon; Verschluss=Schraubverschluss; Verschluss-Schraube=M12; max. Höhe=282 mm; max. Temperaturbeständigkeit=250 °C; max. zul. Last=11.50 kN; vpe=1 St
- Titan HD, 1/2", Ø280, Silikon: Achsabstand=343 mm; Anschluss=1/2''; Anschlußhöhe=26 mm; Artikelnummer=0077925; B=372 mm; Bauart=zweiteilig; Baustoffklasse=B2; Brandschutz=RAL GZ 656; Breite=372 mm; D=280 mm; D0=292 mm; DF2=20 mm  [stored 0.0656168 ft]; Dämmstärke=6 mm  [stored 0.019685 ft]; EAN=4250928405456; Fabrikat=MEFA; Farbe Schalldämmeinlage=rot; Gewicht=2.55 kg; Gewicht pro Bauteil=2.55 kg; H=317 mm; Höhe=317 mm; Kurztext1=Rohrschelle Titan HD 50x5,0; Kurztext2=280 mm 1/2'' Silikon; Material=Stahl; Material Schalldämmeinlage=Silikon; Materialmaße=50x5,0 mm; Materialname=S235; Mengeneinheit=St; Oberflaeche=galvanisch verzinkt; R=146 mm; RM=151 mm; Rohraußendurchmesser=280 mm; Rohraußendurchmesser Zoll=Zoll; S=343 mm; Schalldämmeinlage=Silikon; Verschluss=Schraubverschluss; Verschluss-Schraube=M12; max. Höhe=317 mm; max. Temperaturbeständigkeit=250 °C; max. zul. Last=11.50 kN; vpe=1 St
- Titan HD, 1/2", Ø298, Silikon: Achsabstand=361 mm; Anschluss=1/2''; Anschlußhöhe=26 mm; Artikelnummer=0077933; B=390 mm; Bauart=zweiteilig; Baustoffklasse=B2; Brandschutz=RAL GZ 656; Breite=390 mm; D=298 mm; D0=310 mm; DF2=20 mm  [stored 0.0656168 ft]; Dämmstärke=6 mm  [stored 0.019685 ft]; EAN=4250928405463; Fabrikat=MEFA; Farbe Schalldämmeinlage=rot; Gewicht=2.69 kg; Gewicht pro Bauteil=2.69 kg; H=335 mm; Höhe=335 mm; Kurztext1=Rohrschelle Titan HD 50x5,0; Kurztext2=298 mm 1/2'' Silikon; Material=Stahl; Material Schalldämmeinlage=Silikon; Materialmaße=50x5,0 mm; Materialname=S235; Mengeneinheit=St; Oberflaeche=galvanisch verzinkt; R=155 mm; RM=160 mm; Rohraußendurchmesser=298 mm; Rohraußendurchmesser Zoll=Zoll; S=361 mm; Schalldämmeinlage=Silikon; Verschluss=Schraubverschluss; Verschluss-Schraube=M12; max. Höhe=335 mm; max. Temperaturbeständigkeit=250 °C; max. zul. Last=11.50 kN; vpe=1 St

note: [stored X ft] marks values corroborated as IEEE doubles in the binary element streams (Revit-internal decimal feet)

## geometry (parser evidence)
native form markers: Sweep x1
no freeform markers — native parametric forms only
